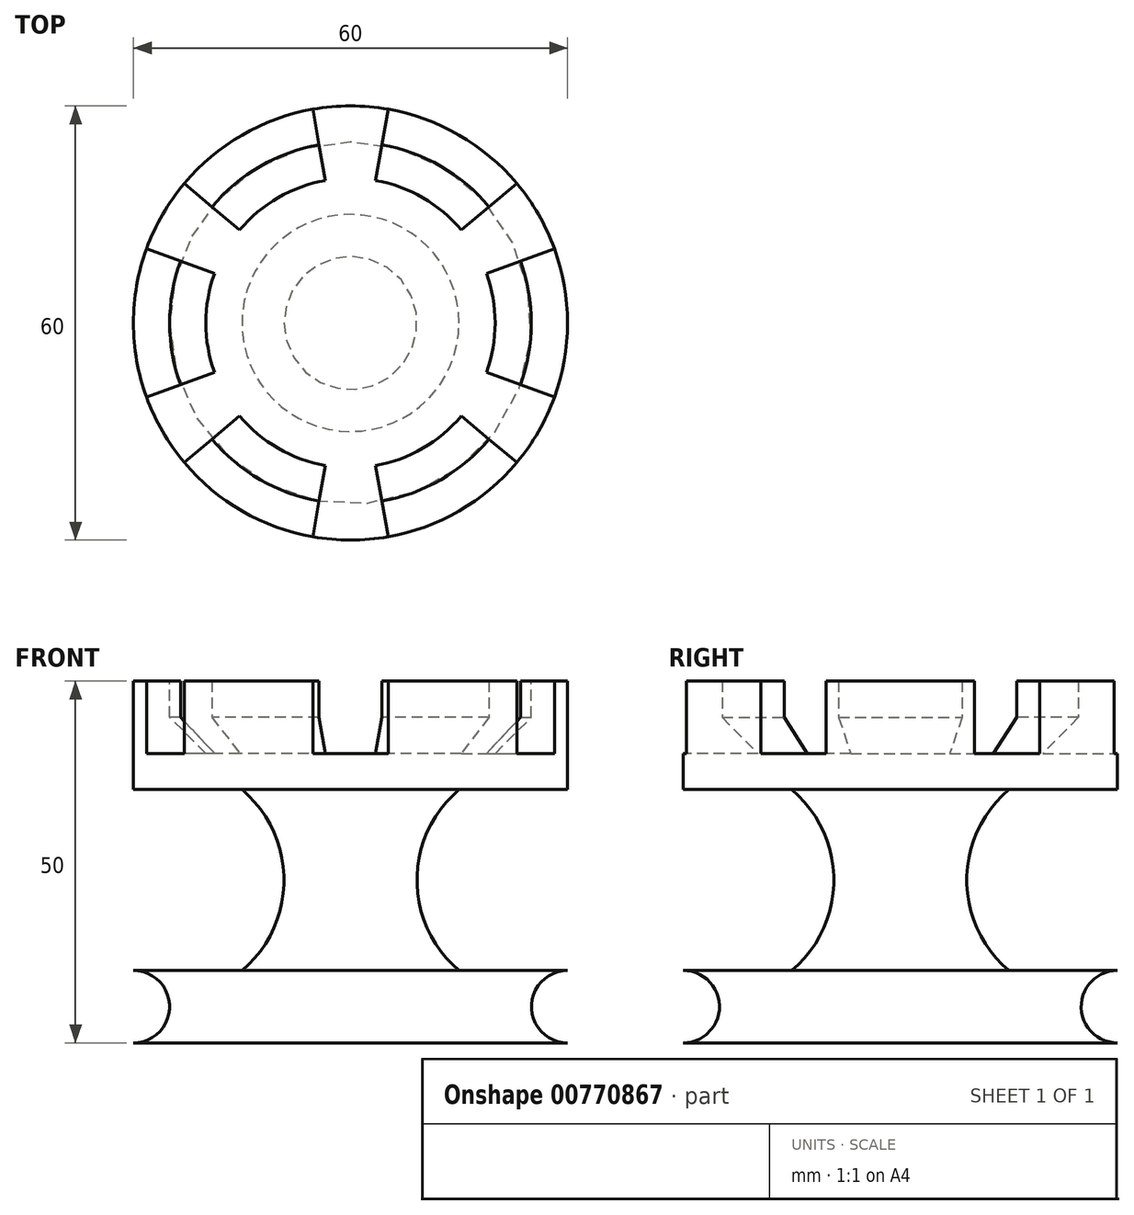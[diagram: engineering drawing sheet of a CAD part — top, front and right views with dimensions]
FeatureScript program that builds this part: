
annotation { "Feature Type Name" : "Feature", "Feature Type Description" : "" }
export const myFeature = defineFeature(function(context is Context, id is Id, definition is map)
    precondition{}
    {
        {
            var Q0;
            Q0=qCreatedBy(makeId("Front.planeOp"),FACE);
            var sketch = newSketch(context, id + "F0", { "sketchPlane" : qUnion([Q0])});
            skLineSegment(sketch, "E0.bottom", {"start": v(0, 0) * mm, "end": v(15, 0) * mm});
            skLineSegment(sketch, "E0.left", {"start": v(0, 0) * mm, "end": v(0, 35) * mm});
            skLineSegment(sketch, "E1.bottom", {"start": v(15, 35) * mm, "end": v(30, 35) * mm});
            skLineSegment(sketch, "E1.top", {"start": v(0, 50) * mm, "end": v(30, 50) * mm});
            skLineSegment(sketch, "E1.left", {"start": v(0, 35) * mm, "end": v(0, 50) * mm});
            skLineSegment(sketch, "E1.right", {"start": v(30, 35) * mm, "end": v(30, 50) * mm});
            skLineSegment(sketch, "E2.bottom", {"start": v(0, 0) * mm, "end": v(30, 0) * mm});
            skLineSegment(sketch, "E2.top", {"start": v(15, 10) * mm, "end": v(30, 10) * mm});
            skLineSegment(sketch, "E2.left", {"start": v(0, 0) * mm, "end": v(0, 10) * mm});
            skLineSegment(sketch, "E2.right", {"start": v(30, 0) * mm, "end": v(30, 10) * mm});
            skArc(sketch, "E3", {"start": v(15, 35) * mm, "mid": v(9.19, 22.5) * mm, "end": v(15, 10) * mm});
            skArc(sketch, "E4", {"start": v(30, 10) * mm, "mid": v(25, 5) * mm, "end": v(30, 0) * mm});
            skSolve(sketch);
        }
        {
            var Q0;
            Q0=makeQuery(id+"F0.imprint","IMPRINT",FACE,{"disambiguationData":[TD([[makeQuery(id+"F0.imprint","IMPRINT",EDGE,{"derivedFrom":sQuery(id+"F0.wireOp",EDGE,"E0.left")}),-1.0]])]});
            var Q1;
            Q1=sQuery(id+"F0.wireOp",EDGE,"E1.left");
            revolve(context, id + "F1", {"surfaceOperationType" : NewSurfaceOperationType.NEW, "entities" : qUnion([Q0]), "axis" : qUnion([Q1]), "revolveType" : RevolveType.FULL});
        }
        {
            var Q0;
            Q0=makeQuery(id+"F1.opRevolve","SWEPT_FACE",FACE,{"disambiguationData":[OSD([sQuery(id+"F0.wireOp",EDGE,"E1.top")])]});
            var sketch = newSketch(context, id + "F2", { "sketchPlane" : qUnion([Q0])});
            skCircle(sketch, "E5", {"center": v(0, 0) * mm, "radius": 25 * mm});
            skSolve(sketch);
        }
        {
            var Q0;
            Q0=makeQuery(id+"F2.imprint","IMPRINT",FACE,{"disambiguationData":[TD([[makeQuery(id+"F2.imprint","IMPRINT",EDGE,{"derivedFrom":sQuery(id+"F2.wireOp",EDGE,"E5")}),1.0]])]});
            extrude(context, id + "F3", {"entities" : qUnion([Q0]), "operationType" : NewBodyOperationType.REMOVE, "oppositeDirection" : true, "depth" : 10 * mm, "offsetDistance" : 25 * mm});
        }
        {
            var Q0;
            Q0=makeQuery(id+"F3.boolean.opBoolean","COPY",FACE,{"derivedFrom":makeQuery(id+"F3.opExtrude","CAP_FACE",FACE,{"disambiguationData":[OSD([sQuery(id+"F2.wireOp",EDGE,"E5")])],"isStart":false})});
            var sketch = newSketch(context, id + "F4", { "sketchPlane" : qUnion([Q0])});
            skLineSegment(sketch, "E6", {"start": v(4.34, 24.62) * mm, "end": v(5.2, 29.54) * mm});
            skLineSegment(sketch, "E7", {"start": v(-4.34, 24.62) * mm, "end": v(-5.2, 29.54) * mm});
            skArc(sketch, "E8", {"start": v(4.34, 24.62) * mm, "mid": v(0, 25) * mm, "end": v(-4.34, 24.62) * mm});
            skArc(sketch, "E9", {"start": v(5.2, 29.54) * mm, "mid": v(0, 30) * mm, "end": v(-5.2, 29.54) * mm});
            skArc(sketch, "E10.1.0", {"start": v(-22.98, 19.28) * mm, "mid": v(-25.98, 15) * mm, "end": v(-28.2, 10.26) * mm});
            skLineSegment(sketch, "E10.1.1", {"start": v(-23.5, 8.55) * mm, "end": v(-28.2, 10.26) * mm});
            skLineSegment(sketch, "E10.1.2", {"start": v(-19.15, 16.07) * mm, "end": v(-22.98, 19.28) * mm});
            skArc(sketch, "E10.1.3", {"start": v(-19.15, 16.07) * mm, "mid": v(-21.65, 12.5) * mm, "end": v(-23.5, 8.55) * mm});
            skArc(sketch, "E10.2.0", {"start": v(-28.2, -10.26) * mm, "mid": v(-25.98, -15) * mm, "end": v(-22.98, -19.28) * mm});
            skLineSegment(sketch, "E10.2.1", {"start": v(-19.15, -16.07) * mm, "end": v(-22.98, -19.28) * mm});
            skLineSegment(sketch, "E10.2.2", {"start": v(-23.5, -8.55) * mm, "end": v(-28.2, -10.26) * mm});
            skArc(sketch, "E10.2.3", {"start": v(-23.5, -8.55) * mm, "mid": v(-21.65, -12.5) * mm, "end": v(-19.15, -16.07) * mm});
            skArc(sketch, "E10.3.0", {"start": v(-5.2, -29.54) * mm, "mid": v(0, -30) * mm, "end": v(5.2, -29.54) * mm});
            skLineSegment(sketch, "E10.3.1", {"start": v(4.34, -24.62) * mm, "end": v(5.2, -29.54) * mm});
            skLineSegment(sketch, "E10.3.2", {"start": v(-4.34, -24.62) * mm, "end": v(-5.2, -29.54) * mm});
            skArc(sketch, "E10.3.3", {"start": v(-4.34, -24.62) * mm, "mid": v(0, -25) * mm, "end": v(4.34, -24.62) * mm});
            skArc(sketch, "E10.4.0", {"start": v(22.98, -19.28) * mm, "mid": v(25.98, -15) * mm, "end": v(28.2, -10.26) * mm});
            skLineSegment(sketch, "E10.4.1", {"start": v(23.5, -8.55) * mm, "end": v(28.2, -10.26) * mm});
            skLineSegment(sketch, "E10.4.2", {"start": v(19.15, -16.07) * mm, "end": v(22.98, -19.28) * mm});
            skArc(sketch, "E10.4.3", {"start": v(19.15, -16.07) * mm, "mid": v(21.65, -12.5) * mm, "end": v(23.5, -8.55) * mm});
            skArc(sketch, "E10.5.0", {"start": v(28.2, 10.26) * mm, "mid": v(25.98, 15) * mm, "end": v(22.98, 19.28) * mm});
            skLineSegment(sketch, "E10.5.1", {"start": v(19.15, 16.07) * mm, "end": v(22.98, 19.28) * mm});
            skLineSegment(sketch, "E10.5.2", {"start": v(23.5, 8.55) * mm, "end": v(28.2, 10.26) * mm});
            skArc(sketch, "E10.5.3", {"start": v(23.5, 8.55) * mm, "mid": v(21.65, 12.5) * mm, "end": v(19.15, 16.07) * mm});
            skSolve(sketch);
        }
        {
            var Q0;
            Q0 = qSketchRegion(id + "F4", true);
            extrude(context, id + "F5", {"entities" : qUnion([Q0]), "operationType" : NewBodyOperationType.REMOVE, "depth" : 42.2 * mm, "offsetDistance" : 25 * mm});
        }
        {
            var Q0;
            {var subQ1=sQuery(id+"F2.wireOp",EDGE,"E5");var subQ2=sQuery(id+"F4.wireOp",EDGE,"E10.4.1");Q0=makeQuery(id+"F5.boolean.opBoolean","SPLIT",EDGE,{"disambiguationData":[TD([makeQuery(id+"F5.opExtrude","SWEPT_FACE",FACE,{"disambiguationData":[OSD([subQ2])]})])],"derivedFrom":makeQuery(id+"F3.boolean.opBoolean","COPY",EDGE,{"derivedFrom":makeQuery(id+"F3.opExtrude","CAP_EDGE",EDGE,{"disambiguationData":[OSD([subQ1])],"isStart":false})})});}
            var Q1;
            {var subQ0=sQuery(id+"F2.wireOp",EDGE,"E5");var subQ2=sQuery(id+"F4.wireOp",EDGE,"E10.2.1");Q1=makeQuery(id+"F5.boolean.opBoolean","SPLIT",EDGE,{"disambiguationData":[TD([makeQuery(id+"F5.opExtrude","SWEPT_FACE",FACE,{"disambiguationData":[OSD([subQ2])]})])],"derivedFrom":makeQuery(id+"F3.boolean.opBoolean","COPY",EDGE,{"derivedFrom":makeQuery(id+"F3.opExtrude","CAP_EDGE",EDGE,{"disambiguationData":[OSD([subQ0])],"isStart":false})})});}
            var Q2;
            {var subQ0=sQuery(id+"F2.wireOp",EDGE,"E5");var subQ1=sQuery(id+"F4.wireOp",EDGE,"E10.1.1");Q2=makeQuery(id+"F5.boolean.opBoolean","SPLIT",EDGE,{"disambiguationData":[TD([makeQuery(id+"F5.opExtrude","SWEPT_FACE",FACE,{"disambiguationData":[OSD([subQ1])]})])],"derivedFrom":makeQuery(id+"F3.boolean.opBoolean","COPY",EDGE,{"derivedFrom":makeQuery(id+"F3.opExtrude","CAP_EDGE",EDGE,{"disambiguationData":[OSD([subQ0])],"isStart":false})})});}
            var Q3;
            {var subQ0=sQuery(id+"F4.wireOp",EDGE,"E7");var subQ1=sQuery(id+"F2.wireOp",EDGE,"E5");Q3=makeQuery(id+"F5.boolean.opBoolean","SPLIT",EDGE,{"disambiguationData":[TD([makeQuery(id+"F5.opExtrude","SWEPT_FACE",FACE,{"disambiguationData":[OSD([subQ0])]})])],"derivedFrom":makeQuery(id+"F3.boolean.opBoolean","COPY",EDGE,{"derivedFrom":makeQuery(id+"F3.opExtrude","CAP_EDGE",EDGE,{"disambiguationData":[OSD([subQ1])],"isStart":false})})});}
            var Q4;
            {var subQ0=sQuery(id+"F4.wireOp",EDGE,"E6");var subQ1=sQuery(id+"F2.wireOp",EDGE,"E5");Q4=makeQuery(id+"F5.boolean.opBoolean","SPLIT",EDGE,{"disambiguationData":[TD([makeQuery(id+"F5.opExtrude","SWEPT_FACE",FACE,{"disambiguationData":[OSD([subQ0])]})])],"derivedFrom":makeQuery(id+"F3.boolean.opBoolean","COPY",EDGE,{"derivedFrom":makeQuery(id+"F3.opExtrude","CAP_EDGE",EDGE,{"disambiguationData":[OSD([subQ1])],"isStart":false})})});}
            var Q5;
            {var subQ0=sQuery(id+"F2.wireOp",EDGE,"E5");Q5=makeQuery(id+"F5.boolean.opBoolean","SPLIT",EDGE,{"disambiguationData":[TD([makeQuery(id+"F5.opExtrude","SWEPT_FACE",FACE,{"disambiguationData":[OSD([sQuery(id+"F4.wireOp",EDGE,"E7")])]})])],"derivedFrom":makeQuery(id+"F3.boolean.opBoolean","COPY",EDGE,{"derivedFrom":makeQuery(id+"F3.opExtrude","CAP_EDGE",EDGE,{"disambiguationData":[OSD([subQ0])],"isStart":true})})});}
            var Q6;
            {var subQ0=sQuery(id+"F2.wireOp",EDGE,"E5");Q6=makeQuery(id+"F5.boolean.opBoolean","SPLIT",EDGE,{"disambiguationData":[TD([makeQuery(id+"F5.opExtrude","SWEPT_FACE",FACE,{"disambiguationData":[OSD([sQuery(id+"F4.wireOp",EDGE,"E6")])]})])],"derivedFrom":makeQuery(id+"F3.boolean.opBoolean","COPY",EDGE,{"derivedFrom":makeQuery(id+"F3.opExtrude","CAP_EDGE",EDGE,{"disambiguationData":[OSD([subQ0])],"isStart":true})})});}
            var Q7;
            {var subQ0=sQuery(id+"F2.wireOp",EDGE,"E5");Q7=makeQuery(id+"F5.boolean.opBoolean","SPLIT",EDGE,{"disambiguationData":[TD([makeQuery(id+"F5.opExtrude","SWEPT_FACE",FACE,{"disambiguationData":[OSD([sQuery(id+"F4.wireOp",EDGE,"E10.4.1")])]})])],"derivedFrom":makeQuery(id+"F3.boolean.opBoolean","COPY",EDGE,{"derivedFrom":makeQuery(id+"F3.opExtrude","CAP_EDGE",EDGE,{"disambiguationData":[OSD([subQ0])],"isStart":true})})});}
            var Q8;
            {var subQ0=sQuery(id+"F2.wireOp",EDGE,"E5");var subQ1=sQuery(id+"F4.wireOp",EDGE,"E10.3.1");Q8=makeQuery(id+"F5.boolean.opBoolean","SPLIT",EDGE,{"disambiguationData":[TD([makeQuery(id+"F5.opExtrude","SWEPT_FACE",FACE,{"disambiguationData":[OSD([subQ1])]})])],"derivedFrom":makeQuery(id+"F3.boolean.opBoolean","COPY",EDGE,{"derivedFrom":makeQuery(id+"F3.opExtrude","CAP_EDGE",EDGE,{"disambiguationData":[OSD([subQ0])],"isStart":false})})});}
            var Q9;
            {var subQ0=sQuery(id+"F2.wireOp",EDGE,"E5");Q9=makeQuery(id+"F5.boolean.opBoolean","SPLIT",EDGE,{"disambiguationData":[TD([makeQuery(id+"F5.opExtrude","SWEPT_FACE",FACE,{"disambiguationData":[OSD([sQuery(id+"F4.wireOp",EDGE,"E10.3.1")])]})])],"derivedFrom":makeQuery(id+"F3.boolean.opBoolean","COPY",EDGE,{"derivedFrom":makeQuery(id+"F3.opExtrude","CAP_EDGE",EDGE,{"disambiguationData":[OSD([subQ0])],"isStart":true})})});}
            var Q10;
            {var subQ0=sQuery(id+"F2.wireOp",EDGE,"E5");Q10=makeQuery(id+"F5.boolean.opBoolean","SPLIT",EDGE,{"disambiguationData":[TD([makeQuery(id+"F5.opExtrude","SWEPT_FACE",FACE,{"disambiguationData":[OSD([sQuery(id+"F4.wireOp",EDGE,"E10.2.1")])]})])],"derivedFrom":makeQuery(id+"F3.boolean.opBoolean","COPY",EDGE,{"derivedFrom":makeQuery(id+"F3.opExtrude","CAP_EDGE",EDGE,{"disambiguationData":[OSD([subQ0])],"isStart":true})})});}
            var Q11;
            {var subQ0=sQuery(id+"F2.wireOp",EDGE,"E5");Q11=makeQuery(id+"F5.boolean.opBoolean","SPLIT",EDGE,{"disambiguationData":[TD([makeQuery(id+"F5.opExtrude","SWEPT_FACE",FACE,{"disambiguationData":[OSD([sQuery(id+"F4.wireOp",EDGE,"E10.1.1")])]})])],"derivedFrom":makeQuery(id+"F3.boolean.opBoolean","COPY",EDGE,{"derivedFrom":makeQuery(id+"F3.opExtrude","CAP_EDGE",EDGE,{"disambiguationData":[OSD([subQ0])],"isStart":true})})});}
            chamfer(context, id + "F6", {"entities" : qUnion([Q0, Q1, Q2, Q3, Q4, Q5, Q6, Q7, Q8, Q9, Q10, Q11]), "width" : 5 * mm, "tangentPropagation" : true});
        }
    });
